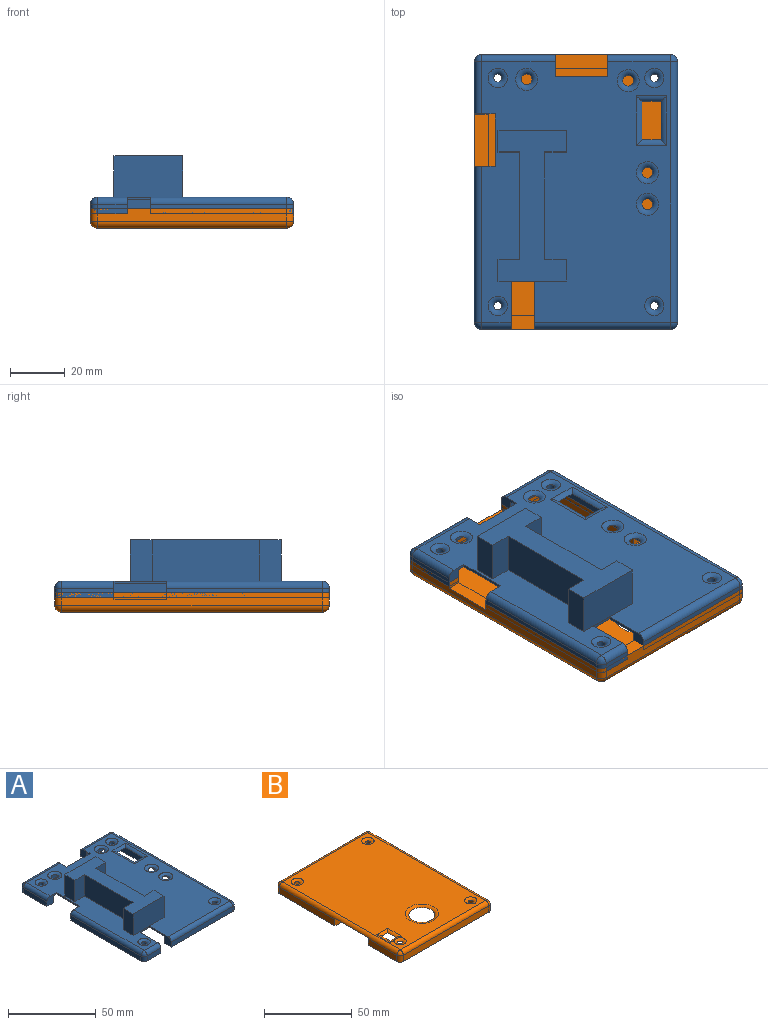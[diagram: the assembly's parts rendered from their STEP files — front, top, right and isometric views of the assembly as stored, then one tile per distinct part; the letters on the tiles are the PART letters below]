
ASSEMBLY  parts=2 mates=1
PART A: 84 faces, bbox 74x100x21 mm
  f0: plane 90x64mm, normal (0,0,-1), area 5230.7mm2, adj f1,f2,f4,f8,f12,f21,f22,f27
  f1: plane 90x5mm, normal (-1,0,0), area 391.5mm2, adj f0,f5,f8,f21,f63,f66,f68,f70
  f2: plane 24.46x5mm, normal (0,-1,0), area 93.1mm2, adj f0,f9,f12,f50,f55,f58
  f3: plane 49.62x3.46mm, normal (0,-1,0), area 171.7mm2, adj f5,f14,f44,f53
  f4: plane 8.46x5mm, normal (0,1,0), area 13.1mm2, adj f0,f22,f24,f54,f59,f62
  f5: plane 100x52.16mm, normal (0,0,-1), area 835.4mm2, adj f1,f3,f7,f8,f14,f15,f16,f21
  f6: cylinder r=2.54mm len=10.92mm, axis (1,0,0), area 43.6mm2, adj f23,f25,f45,f54
  f7: plane 22.95x3.46mm, normal (0,1,0), area 79.4mm2, adj f5,f10,f16,f51
  f8: plane 20.49x5mm, normal (0,-1,0), area 73.2mm2, adj f0,f1,f5,f51,f64,f66
  f9: plane 29.46x21.59mm, normal (0,0,-1), area 228.9mm2, adj f2,f12,f17,f18,f19,f48,f50
  f10: cylinder r=2.54mm len=22.95mm, axis (-1,0,0), area 91.6mm2, adj f7,f25,f38,f51
  f11: plane 56.82x3.46mm, normal (-1,0,0), area 196.6mm2, adj f20,f24,f43,f47
  f12: plane 16.59x5mm, normal (1,0,0), area 53.7mm2, adj f0,f2,f9,f48,f56,f58
  f13: cylinder r=2.54mm len=19.05mm, axis (0,-1,0), area 76mm2, adj f19,f25,f41,f48
  f14: cylinder r=2.54mm len=3.46mm, axis (0,0,1), area 13.8mm2, adj f3,f5,f15,f42
  f15: plane 94.92x3.46mm, normal (1,0,0), area 328.4mm2, adj f5,f14,f16,f40
  f16: cylinder r=2.54mm len=3.46mm, axis (0,0,1), area 13.8mm2, adj f5,f7,f15,f38
  f17: plane 26.92x3.46mm, normal (0,1,0), area 93.2mm2, adj f9,f18,f39,f50
  f18: cylinder r=2.54mm len=3.46mm, axis (0,0,1), area 13.8mm2, adj f9,f17,f19,f41
  f19: plane 19.05x3.46mm, normal (-1,0,0), area 65.9mm2, adj f9,f13,f18,f48
  f20: cylinder r=2.54mm len=3.46mm, axis (0,0,1), area 13.8mm2, adj f11,f23,f24,f45
  f21: plane 47.16x5mm, normal (0,1,0), area 206.5mm2, adj f0,f1,f5,f53,f67,f70
  f22: plane 54.36x5mm, normal (1,0,0), area 242.5mm2, adj f0,f4,f24,f47,f60,f62
  f23: plane 10.92x3.46mm, normal (0,-1,0), area 37.8mm2, adj f6,f20,f24,f54
  f24: plane 59.36x13.46mm, normal (0,0,-1), area 337.7mm2, adj f4,f11,f20,f22,f23,f47,f54
  f25: plane 94.92x68.92mm, normal (0,0,1), area 4906.6mm2, adj f6,f10,f13,f26,f27,f28,f29,f30
  f26: torus R=3.52mm, axis (0,0,1), area 35.7mm2, adj f25,f61
  f27: torus R=4.02mm, axis (0,0,1), area 43mm2, adj f0,f25
  f28: cylinder r=2.54mm len=18.04mm, axis (0,-1,0), area 37mm2, adj f0,f25,f29,f30
  f29: cylinder r=2.54mm len=11.04mm, axis (1,0,0), area 20.7mm2, adj f0,f25,f28,f31
  f30: cylinder r=2.54mm len=11.04mm, axis (1,0,0), area 20.7mm2, adj f0,f25,f28,f31
  f31: cylinder r=2.54mm len=18.04mm, axis (0,-1,0), area 37mm2, adj f0,f25,f29,f30
  f32: torus R=3.52mm, axis (0,0,1), area 35.7mm2, adj f25,f65
  f33: torus R=4.02mm, axis (0,0,1), area 43mm2, adj f0,f25
  f34: torus R=4.02mm, axis (0,0,1), area 43mm2, adj f0,f25
  f35: torus R=3.52mm, axis (0,0,1), area 35.7mm2, adj f25,f57
  f36: torus R=4.02mm, axis (0,0,1), area 43mm2, adj f0,f25
  f37: torus R=3.52mm, axis (0,0,1), area 35.7mm2, adj f25,f69
  f38: sphere r=2.54mm, area 10.1mm2, adj f10,f16,f40
  f39: cylinder r=2.54mm len=26.92mm, axis (-1,0,0), area 107.4mm2, adj f17,f25,f41,f50
  f40: cylinder r=2.54mm len=94.92mm, axis (0,1,0), area 378.7mm2, adj f15,f25,f38,f42
  f41: sphere r=2.54mm, area 10.1mm2, adj f13,f18,f39
  f42: sphere r=2.54mm, area 10.1mm2, adj f14,f40,f44
  f43: cylinder r=2.54mm len=56.82mm, axis (0,-1,0), area 226.7mm2, adj f11,f25,f45,f47
  f44: cylinder r=2.54mm len=49.62mm, axis (1,0,0), area 198mm2, adj f3,f25,f42,f53
  f45: sphere r=2.54mm, area 10.1mm2, adj f6,f20,f43
  f46: plane 19.05x1mm, normal (-1,0,0), area 19mm2, adj f0,f25,f47,f48
  f47: plane 7.62x6mm, normal (0,1,0), area 31.2mm2, adj f0,f11,f22,f24,f25,f43,f46
  f48: plane 7.62x6mm, normal (0,-1,0), area 31.2mm2, adj f0,f9,f12,f13,f19,f25,f46
  f49: plane 19.05x1mm, normal (0,1,0), area 19mm2, adj f0,f25,f50,f51
  f50: plane 8x6mm, normal (1,0,0), area 31.6mm2, adj f0,f2,f9,f17,f25,f39,f49
  f51: plane 8x6mm, normal (-1,0,0), area 31.6mm2, adj f0,f5,f7,f8,f10,f25,f49
  f52: plane 8.38x1mm, normal (0,-1,0), area 8.4mm2, adj f0,f25,f53,f54
  f53: plane 17.53x6mm, normal (-1,0,0), area 41.1mm2, adj f0,f3,f5,f21,f25,f44,f52
  f54: plane 17.53x6mm, normal (1,0,0), area 41.1mm2, adj f0,f4,f6,f23,f24,f25,f52
  f55: plane 6.5x4.5mm, normal (1,0,0), area 29.2mm2, adj f0,f2,f56,f58
  f56: plane 6.5x4.5mm, normal (0,-1,0), area 29.2mm2, adj f0,f12,f55,f58
  f57: cylinder r=1.5mm len=4.5mm, axis (0,0,1), area 42.4mm2, adj f35,f58
  f58: plane 6.5x6.5mm, normal (0,0,-1), area 35.2mm2, adj f2,f12,f55,f56,f57
  f59: plane 6.5x4.5mm, normal (1,0,0), area 29.2mm2, adj f0,f4,f60,f62
  f60: plane 6.5x4.5mm, normal (0,1,0), area 29.2mm2, adj f0,f22,f59,f62
  f61: cylinder r=1.5mm len=4.5mm, axis (0,0,1), area 42.4mm2, adj f26,f62
  f62: plane 6.5x6.5mm, normal (0,0,-1), area 35.2mm2, adj f4,f22,f59,f60,f61
  f63: plane 6.5x4.5mm, normal (0,-1,0), area 29.2mm2, adj f0,f1,f64,f66
  f64: plane 6.5x4.5mm, normal (-1,0,0), area 29.2mm2, adj f0,f8,f63,f66
  f65: cylinder r=1.5mm len=4.5mm, axis (0,0,1), area 42.4mm2, adj f32,f66
  f66: plane 6.5x6.5mm, normal (0,0,-1), area 35.2mm2, adj f1,f8,f63,f64,f65
  f67: plane 6.5x4.5mm, normal (-1,0,0), area 29.2mm2, adj f0,f21,f68,f70
  f68: plane 6.5x4.5mm, normal (0,1,0), area 29.2mm2, adj f0,f1,f67,f70
  f69: cylinder r=1.5mm len=4.5mm, axis (0,0,1), area 42.4mm2, adj f37,f70
  f70: plane 6.5x6.5mm, normal (0,0,-1), area 35.2mm2, adj f1,f21,f67,f68,f69
  f71: plane 39x15mm, normal (-1,0,0), area 585mm2, adj f25,f72,f82,f83
  f72: plane 15x8mm, normal (0,1,0), area 120mm2, adj f25,f71,f73,f83
  f73: plane 15x8mm, normal (-1,0,0), area 120mm2, adj f25,f72,f74,f83
  f74: plane 25x15mm, normal (0,-1,0), area 375mm2, adj f25,f73,f75,f83
  f75: plane 15x8mm, normal (1,0,0), area 120mm2, adj f25,f74,f76,f83
  f76: plane 15x8mm, normal (0,1,0), area 120mm2, adj f25,f75,f77,f83
  f77: plane 39x15mm, normal (1,0,0), area 585mm2, adj f25,f76,f78,f83
  f78: plane 15x8mm, normal (0,-1,0), area 120mm2, adj f25,f77,f79,f83
  f79: plane 15x8mm, normal (1,0,0), area 120mm2, adj f25,f78,f80,f83
  f80: plane 25x15mm, normal (0,1,0), area 375mm2, adj f25,f79,f81,f83
  f81: plane 15x8mm, normal (-1,0,0), area 120mm2, adj f25,f80,f82,f83
  f82: plane 15x8mm, normal (0,-1,0), area 120mm2, adj f25,f71,f81,f83
  f83: plane 55x25mm, normal (0,0,1), area 751mm2, adj f71,f72,f73,f74,f75,f76,f77,f78
PART B: 44 faces, bbox 74x100x7 mm
  f0: plane 90x6mm, normal (-1,0,0), area 491.6mm2, adj f2,f4,f9,f16,f18,f41,f42,f43
  f1: plane 94.92x4.46mm, normal (1,0,0), area 375mm2, adj f2,f11,f12,f16,f30,f41,f42,f43
  f2: plane 29.46x21.59mm, normal (0,0,-1), area 228.9mm2, adj f0,f1,f3,f4,f12,f39,f43
  f3: plane 68.92x4.46mm, normal (0,1,0), area 259mm2, adj f2,f5,f12,f13,f29,f38,f39,f40
  f4: plane 64x6mm, normal (0,-1,0), area 335.6mm2, adj f0,f2,f5,f7,f18,f38,f39,f40
  f5: plane 47.46x25.49mm, normal (0,0,-1), area 338.3mm2, adj f3,f4,f7,f13,f14,f35,f40
  f6: plane 23x4.46mm, normal (-1,0,0), area 102.6mm2, adj f8,f15,f16,f36
  f7: plane 90x6mm, normal (1,0,0), area 405mm2, adj f4,f5,f9,f16,f18,f35,f36,f37
  f8: cylinder r=2.54mm len=94.92mm, axis (0,-1,0), area 364mm2, adj f6,f14,f17,f31,f34,f35,f36,f37
  f9: plane 64x6mm, normal (0,1,0), area 384mm2, adj f0,f7,f16,f18
  f10: plane 68.92x4.46mm, normal (0,-1,0), area 307.4mm2, adj f11,f15,f16,f33
  f11: cylinder r=2.54mm len=4.46mm, axis (0,0,1), area 17.8mm2, adj f1,f10,f16,f32
  f12: cylinder r=2.54mm len=4.46mm, axis (0,0,1), area 17.8mm2, adj f1,f2,f3,f28
  f13: cylinder r=2.54mm len=4.46mm, axis (0,0,1), area 17.8mm2, adj f3,f5,f14,f31
  f14: plane 44.92x4.46mm, normal (-1,0,0), area 200.3mm2, adj f5,f8,f13,f35
  f15: cylinder r=2.54mm len=4.46mm, axis (0,0,1), area 17.8mm2, adj f6,f10,f16,f34
  f16: plane 74x59.36mm, normal (0,0,-1), area 741.7mm2, adj f0,f1,f6,f7,f9,f10,f11,f15
  f17: plane 94.92x68.92mm, normal (0,0,1), area 6003mm2, adj f8,f19,f20,f21,f22,f23,f24,f25
  f18: plane 90x64mm, normal (0,0,-1), area 5520mm2, adj f0,f4,f7,f9,f19,f20,f21,f22
  f19: torus R=3.52mm, axis (0,0,1), area 35.7mm2, adj f17,f18
  f20: torus R=3.52mm, axis (0,0,1), area 35mm2, adj f17,f18,f22
  f21: cylinder r=2.54mm len=11.04mm, axis (0,-1,0), area 21.1mm2, adj f17,f18,f22,f23
  f22: cylinder r=2.54mm len=9.04mm, axis (1,0,0), area 15.7mm2, adj f17,f18,f20,f21,f24
  f23: cylinder r=2.54mm len=9.04mm, axis (1,0,0), area 16.4mm2, adj f17,f18,f21,f24
  f24: cylinder r=2.54mm len=11.04mm, axis (0,-1,0), area 21.1mm2, adj f17,f18,f22,f23
  f25: torus R=9.52mm, axis (0,0,1), area 123.7mm2, adj f17,f18
  f26: torus R=3.52mm, axis (0,0,1), area 35.7mm2, adj f17,f18
  f27: torus R=3.52mm, axis (0,0,1), area 35.7mm2, adj f17,f18
  f28: sphere r=2.54mm, area 10.1mm2, adj f12,f29,f30
  f29: cylinder r=2.54mm len=68.92mm, axis (-1,0,0), area 275mm2, adj f3,f17,f28,f31
  f30: cylinder r=2.54mm len=94.92mm, axis (0,1,0), area 378.7mm2, adj f1,f17,f28,f32
  f31: sphere r=2.54mm, area 10.1mm2, adj f8,f13,f29
  f32: sphere r=2.54mm, area 10.1mm2, adj f11,f30,f33
  f33: cylinder r=2.54mm len=68.92mm, axis (1,0,0), area 275mm2, adj f10,f17,f32,f34
  f34: sphere r=2.54mm, area 10.1mm2, adj f8,f15,f33
  f35: plane 5x5mm, normal (0,-1,0), area 25mm2, adj f5,f7,f8,f14,f37
  f36: plane 5x5mm, normal (0,1,0), area 25mm2, adj f6,f7,f8,f16,f37
  f37: plane 27x4.94mm, normal (0,0,-1), area 133.4mm2, adj f7,f8,f35,f36
  f38: plane 19.05x5mm, normal (0,0,-1), area 95.3mm2, adj f3,f4,f39,f40
  f39: plane 5x2.54mm, normal (-1,0,0), area 12.7mm2, adj f2,f3,f4,f38
  f40: plane 5x2.54mm, normal (1,0,0), area 12.7mm2, adj f3,f4,f5,f38
  f41: plane 19.05x5mm, normal (0,0,-1), area 95.2mm2, adj f0,f1,f42,f43
  f42: plane 5x2.54mm, normal (0,1,0), area 12.7mm2, adj f0,f1,f16,f41
  f43: plane 5x2.54mm, normal (0,-1,0), area 12.7mm2, adj f0,f1,f2,f41
PLACE A t=(-10.64,-28.9,-20.34)mm
PLACE B rot(axis=(0,1,0),180deg) t=(-10.64,-28.9,-31.61)mm
MATE planar A.f11 <-> B.f1  axis (-1,0,0) through (-47.64,-47.95,-24.61)mm
